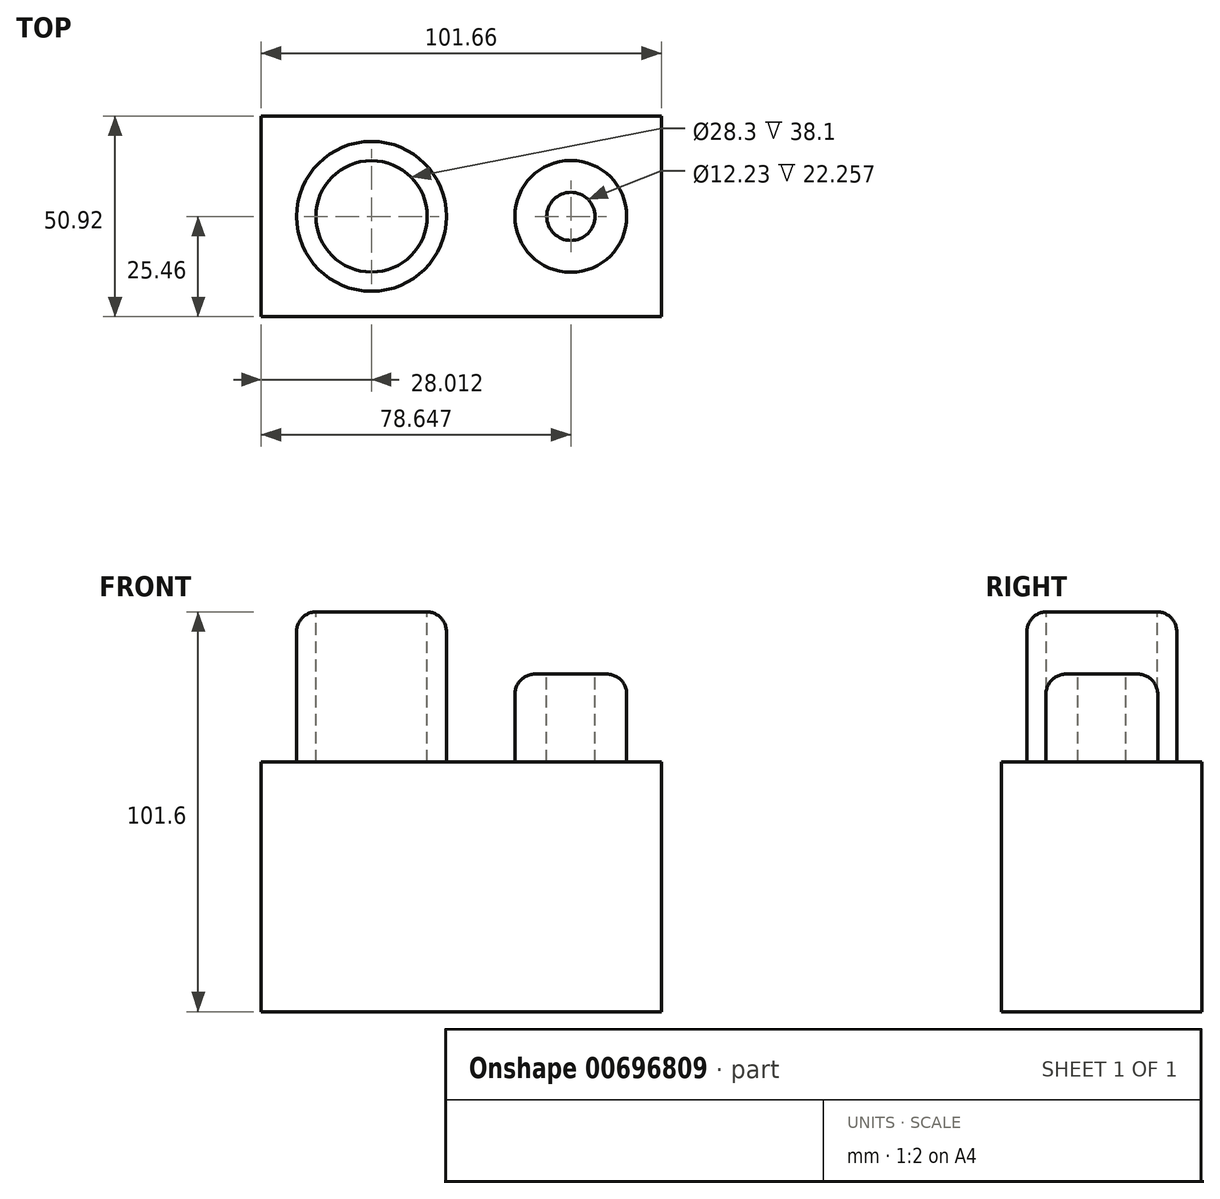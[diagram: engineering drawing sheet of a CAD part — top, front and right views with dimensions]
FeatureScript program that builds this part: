
annotation { "Feature Type Name" : "Feature", "Feature Type Description" : "" }
export const myFeature = defineFeature(function(context is Context, id is Id, definition is map)
    precondition{}
    {
        {
            var Q0;
            Q0=qCreatedBy(makeId("Top.planeOp"),FACE);
            var sketch = newSketch(context, id + "F0", { "sketchPlane" : qUnion([Q0])});
            skLineSegment(sketch, "E0.bottom", {"start": v(50.83, -25.46) * mm, "end": v(-50.83, -25.46) * mm});
            skLineSegment(sketch, "E0.top", {"start": v(50.83, 25.46) * mm, "end": v(-50.83, 25.46) * mm});
            skLineSegment(sketch, "E0.left", {"start": v(50.83, -25.46) * mm, "end": v(50.83, 25.46) * mm});
            skLineSegment(sketch, "E0.right", {"start": v(-50.83, -25.46) * mm, "end": v(-50.83, 25.46) * mm});
            skPoint(sketch, "E0.middle", {"position": v(0, 0) * mm});
            skSolve(sketch);
        }
        {
            var Q0;
            Q0 = qSketchRegion(id + "F0", true);
            extrude(context, id + "F1", {"entities" : qUnion([Q0]), "depth" : 63.5 * mm, "offsetDistance" : 25.4 * mm});
        }
        {
            var Q0;
            Q0=makeQuery(id+"F1.opExtrude","CAP_FACE",FACE,{"disambiguationData":[OSD([sQuery(id+"F0.wireOp",EDGE,"E0.bottom"),sQuery(id+"F0.wireOp",EDGE,"E0.top"),sQuery(id+"F0.wireOp",EDGE,"E0.left"),sQuery(id+"F0.wireOp",EDGE,"E0.right")])],"isStart":false});
            var sketch = newSketch(context, id + "F2", { "sketchPlane" : qUnion([Q0])});
            skCircle(sketch, "E1", {"center": v(-22.82, 0) * mm, "radius": 19.04 * mm});
            skSolve(sketch);
        }
        {
            var Q0;
            Q0 = qSketchRegion(id + "F2", true);
            extrude(context, id + "F3", {"entities" : qUnion([Q0]), "operationType" : NewBodyOperationType.ADD, "depth" : 38.1 * mm, "offsetDistance" : 25.4 * mm});
        }
        {
            var Q0;
            Q0=makeQuery(id+"F3.opExtrude","CAP_FACE",FACE,{"disambiguationData":[OSD([sQuery(id+"F2.wireOp",EDGE,"E1")])],"isStart":false});
            var sketch = newSketch(context, id + "F4", { "sketchPlane" : qUnion([Q0])});
            skCircle(sketch, "E2", {"center": v(-22.82, 0) * mm, "radius": 14.15 * mm});
            skSolve(sketch);
        }
        {
            var Q0;
            Q0=makeQuery(id+"F4.imprint","IMPRINT",FACE,{"disambiguationData":[TD([[makeQuery(id+"F4.imprint","IMPRINT",EDGE,{"derivedFrom":sQuery(id+"F4.wireOp",EDGE,"E2")}),1.0]])]});
            var Q1;
            Q1=makeQuery(id+"F1.opExtrude","CAP_FACE",FACE,{"disambiguationData":[OSD([sQuery(id+"F0.wireOp",EDGE,"E0.bottom"),sQuery(id+"F0.wireOp",EDGE,"E0.top"),sQuery(id+"F0.wireOp",EDGE,"E0.left"),sQuery(id+"F0.wireOp",EDGE,"E0.right")])],"isStart":false});
            extrude(context, id + "F5", {"entities" : qUnion([Q0]), "operationType" : NewBodyOperationType.REMOVE, "endBound" : BoundingType.UP_TO_SURFACE, "oppositeDirection" : true, "depth" : 25.4 * mm, "endBoundEntityFace" : qUnion([Q1]), "offsetDistance" : 25.4 * mm});
        }
        {
            var Q0;
            Q0=qCreatedBy(makeId("Front.planeOp"),FACE);
            var sketch = newSketch(context, id + "F6", { "sketchPlane" : qUnion([Q0])});
            skLineSegment(sketch, "E3", {"start": v(27.82, 85.6) * mm, "end": v(27.82, 32) * mm});
            skLineSegment(sketch, "E4.bottom", {"start": v(21.7, 85.76) * mm, "end": v(13.61, 85.76) * mm});
            skLineSegment(sketch, "E4.top", {"start": v(21.7, 56.05) * mm, "end": v(13.61, 56.05) * mm});
            skLineSegment(sketch, "E4.left", {"start": v(21.7, 85.76) * mm, "end": v(21.7, 56.05) * mm});
            skLineSegment(sketch, "E4.right", {"start": v(13.61, 85.76) * mm, "end": v(13.61, 56.05) * mm});
            skSolve(sketch);
        }
        {
            var Q0;
            Q0=makeQuery(id+"F6.imprint","IMPRINT",FACE,{"disambiguationData":[TD([[makeQuery(id+"F6.imprint","IMPRINT",EDGE,{"derivedFrom":sQuery(id+"F6.wireOp",EDGE,"E4.bottom")}),1.0]])]});
            var Q1;
            Q1=sQuery(id+"F6.wireOp",EDGE,"E3");
            revolve(context, id + "F7", {"operationType" : NewBodyOperationType.ADD, "entities" : qUnion([Q0]), "axis" : qUnion([Q1]), "revolveType" : RevolveType.FULL});
        }
        {
            var Q0;
            Q0=makeQuery(id+"F3.opExtrude","CAP_EDGE",EDGE,{"disambiguationData":[OSD([sQuery(id+"F2.wireOp",EDGE,"E1")])],"isStart":false});
            var Q1;
            Q1=makeQuery(id+"F7.opRevolve","SWEPT_EDGE",EDGE,{"disambiguationData":[OSD([sQuery(id+"F6.wireOp",EDGE,"E4.bottom"),sQuery(id+"F6.wireOp",EDGE,"E4.right")])]});
            fillet(context, id + "F8", {"entities" : qUnion([Q0, Q1]), "radius" : 5.08 * mm, "tangentPropagation" : true, "allowEdgeOverflow" : false});
        }
    });
